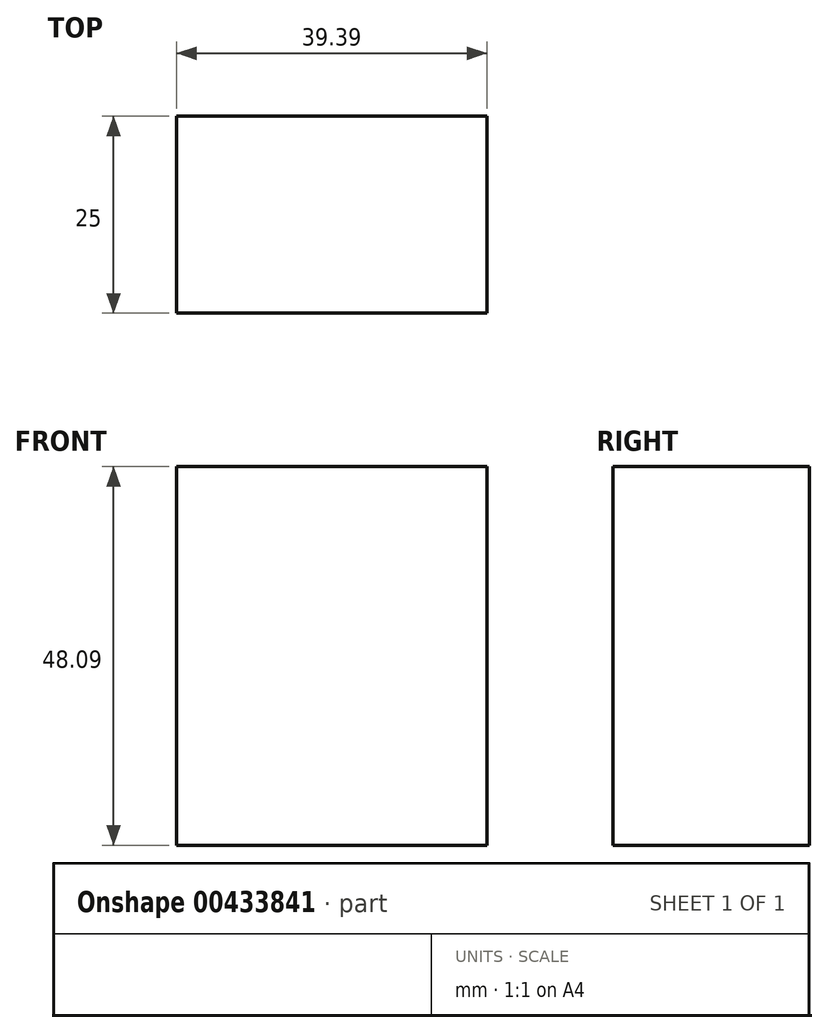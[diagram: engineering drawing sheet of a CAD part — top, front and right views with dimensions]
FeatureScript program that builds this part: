
annotation { "Feature Type Name" : "Feature", "Feature Type Description" : "" }
export const myFeature = defineFeature(function(context is Context, id is Id, definition is map)
    precondition{}
    {
        {
            var Q0;
            Q0=qCreatedBy(makeId("Front.planeOp"),FACE);
            var sketch = newSketch(context, id + "F0", { "sketchPlane" : qUnion([Q0])});
            skLineSegment(sketch, "E0.bottom", {"start": v(-96.13, 10.3) * mm, "end": v(-56.74, 10.3) * mm});
            skLineSegment(sketch, "E0.top", {"start": v(-96.13, 58.39) * mm, "end": v(-56.74, 58.39) * mm});
            skLineSegment(sketch, "E0.left", {"start": v(-96.13, 10.3) * mm, "end": v(-96.13, 58.39) * mm});
            skLineSegment(sketch, "E0.right", {"start": v(-56.74, 10.3) * mm, "end": v(-56.74, 58.39) * mm});
            skPoint(sketch, "E0.middle", {"position": v(-76.44, 34.34) * mm});
            skSolve(sketch);
        }
        {
            var Q0;
            Q0=makeQuery(id+"F0.imprint","IMPRINT",FACE,{"disambiguationData":[TD([[makeQuery(id+"F0.imprint","IMPRINT",EDGE,{"derivedFrom":sQuery(id+"F0.wireOp",EDGE,"E0.bottom")}),1.0]])]});
            extrude(context, id + "F1", {"entities" : qUnion([Q0]), "depth" : 25 * mm});
        }
    });
